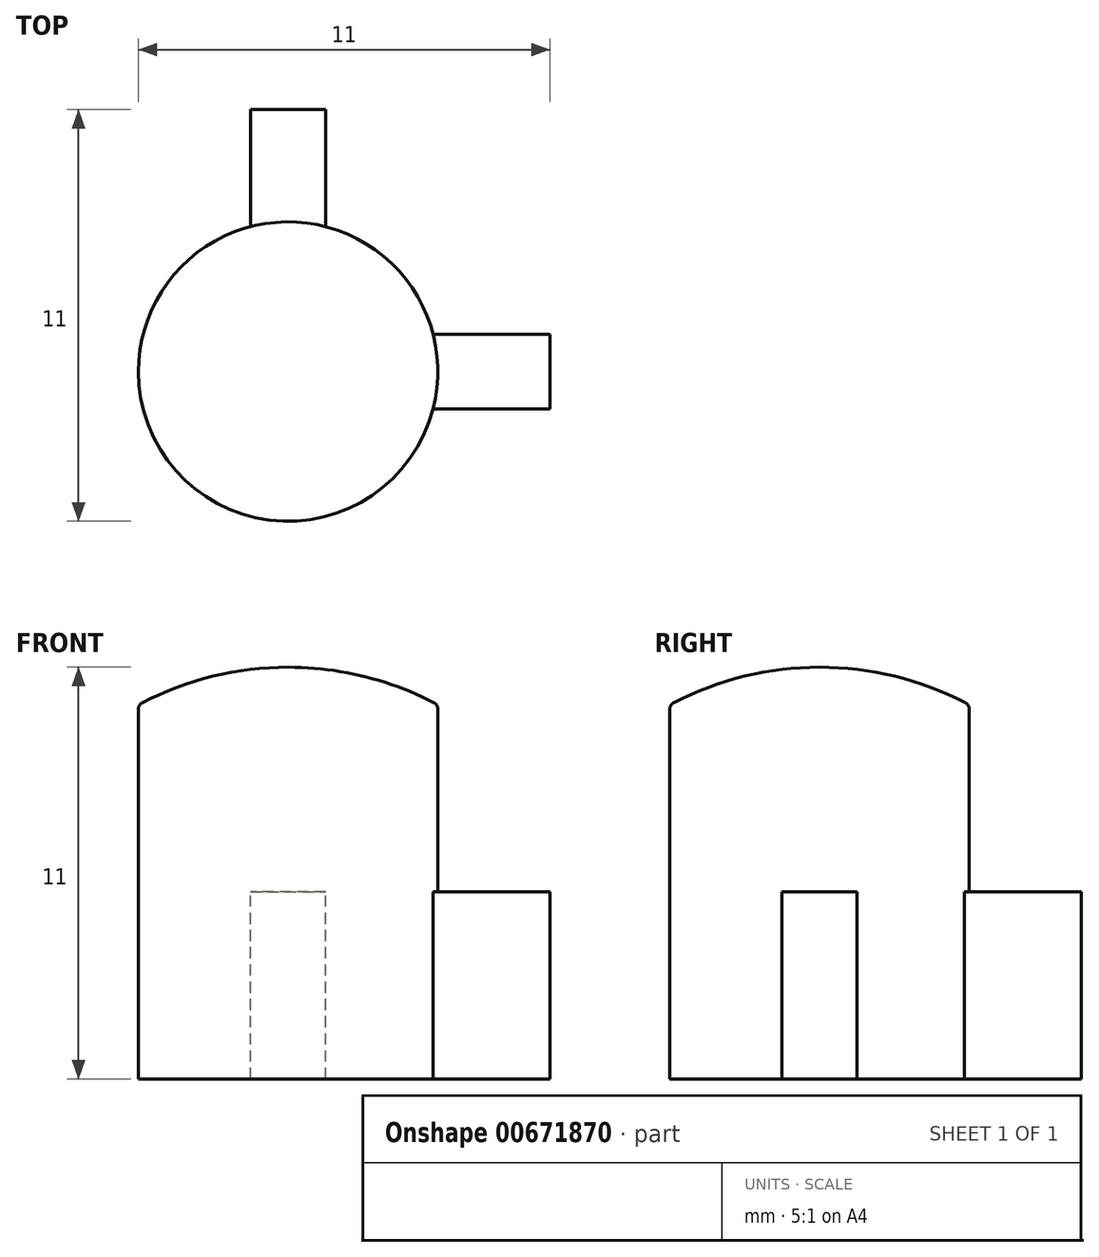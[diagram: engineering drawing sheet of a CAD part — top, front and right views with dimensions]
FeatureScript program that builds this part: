
annotation { "Feature Type Name" : "Feature", "Feature Type Description" : "" }
export const myFeature = defineFeature(function(context is Context, id is Id, definition is map)
    precondition{}
    {
        {
            var Q0;
            Q0=qCreatedBy(makeId("Front.planeOp"),FACE);
            var sketch = newSketch(context, id + "F0", { "sketchPlane" : qUnion([Q0])});
            skLineSegment(sketch, "E0", {"start": v(0, 0) * mm, "end": v(4, 0) * mm});
            skLineSegment(sketch, "E1", {"start": v(4, 0) * mm, "end": v(4, 10) * mm});
            skLineSegment(sketch, "E2", {"start": v(4, 10) * mm, "end": v(0, 10) * mm});
            skLineSegment(sketch, "E3", {"start": v(0, 10) * mm, "end": v(0, 0) * mm});
            skArc(sketch, "E4", {"start": v(0, 9.25) * mm, "mid": v(1.91, 9.44) * mm, "end": v(3.75, 10) * mm});
            skArc(sketch, "E5", {"start": v(4, 10) * mm, "mid": v(2.06, 10.75) * mm, "end": v(0, 11) * mm});
            skLineSegment(sketch, "E6", {"start": v(0, 10) * mm, "end": v(0, 11) * mm});
            skSolve(sketch);
        }
        {
            var Q0;
            {var subQ4=sQuery(id+"F0.wireOp",EDGE,"E0");Q0=makeQuery(id+"F0.imprint","IMPRINT",FACE,{"disambiguationData":[TD([[makeQuery(id+"F0.imprint","IMPRINT",EDGE,{"derivedFrom":subQ4}),1.0]])]});}
            var Q1;
            {var subQ3=sQuery(id+"F0.wireOp",EDGE,"E4");Q1=makeQuery(id+"F0.imprint","IMPRINT",FACE,{"disambiguationData":[TD([[makeQuery(id+"F0.imprint","IMPRINT",EDGE,{"derivedFrom":subQ3}),1.0]])]});}
            var Q2;
            {var subQ0=sQuery(id+"F0.wireOp",EDGE,"E5");Q2=makeQuery(id+"F0.imprint","IMPRINT",FACE,{"disambiguationData":[TD([[makeQuery(id+"F0.imprint","IMPRINT",EDGE,{"derivedFrom":subQ0}),1.0]])]});}
            var Q3;
            Q3=sQuery(id+"F0.wireOp",EDGE,"E3");
            revolve(context, id + "F1", {"entities" : qUnion([Q0, Q1, Q2]), "axis" : qUnion([Q3]), "revolveType" : RevolveType.FULL});
        }
        {
            var Q0;
            Q0=makeQuery(id+"F1.opRevolve","SWEPT_EDGE",EDGE,{"disambiguationData":[OSD([sQuery(id+"F0.wireOp",EDGE,"E2"),sQuery(id+"F0.wireOp",EDGE,"E4")])]});
            var Q1;
            Q1=makeQuery(id+"F1.opRevolve","SWEPT_EDGE",EDGE,{"disambiguationData":[OSD([sQuery(id+"F0.wireOp",EDGE,"E1"),sQuery(id+"F0.wireOp",EDGE,"E2")])]});
            fillet(context, id + "F2", {"entities" : qUnion([Q0, Q1]), "radius" : 0.2 * mm, "tangentPropagation" : true, "allowEdgeOverflow" : false});
        }
        {
            var Q0;
            Q0=qCreatedBy(makeId("Top.planeOp"),FACE);
            var sketch = newSketch(context, id + "F3", { "sketchPlane" : qUnion([Q0])});
            skLineSegment(sketch, "E7.bottom", {"start": v(-1, 0) * mm, "end": v(1, 0) * mm});
            skLineSegment(sketch, "E7.top", {"start": v(-1, 7) * mm, "end": v(1, 7) * mm});
            skLineSegment(sketch, "E7.left", {"start": v(-1, 0) * mm, "end": v(-1, 7) * mm});
            skLineSegment(sketch, "E7.right", {"start": v(1, 0) * mm, "end": v(1, 7) * mm});
            skPoint(sketch, "E7.middle", {"position": v(0, 3.5) * mm});
            skLineSegment(sketch, "E8.bottom", {"start": v(7, 1) * mm, "end": v(0, 1) * mm});
            skLineSegment(sketch, "E8.top", {"start": v(7, -1) * mm, "end": v(0, -1) * mm});
            skLineSegment(sketch, "E8.left", {"start": v(7, 1) * mm, "end": v(7, -1) * mm});
            skLineSegment(sketch, "E8.right", {"start": v(0, 1) * mm, "end": v(0, -1) * mm});
            skPoint(sketch, "E8.middle", {"position": v(3.5, 0) * mm});
            skSolve(sketch);
        }
        {
            var Q0;
            {var subQ1=sQuery(id+"F3.wireOp",EDGE,"E7.top");Q0=makeQuery(id+"F3.imprint","IMPRINT",FACE,{"disambiguationData":[TD([[makeQuery(id+"F3.imprint","IMPRINT",EDGE,{"derivedFrom":subQ1}),-1.0]])]});}
            var Q1;
            {var subQ0=sQuery(id+"F3.wireOp",EDGE,"E8.top");Q1=makeQuery(id+"F3.imprint","IMPRINT",FACE,{"disambiguationData":[TD([[makeQuery(id+"F3.imprint","IMPRINT",EDGE,{"derivedFrom":subQ0}),-1.0]])]});}
            extrude(context, id + "F4", {"entities" : qUnion([Q0, Q1]), "operationType" : NewBodyOperationType.ADD, "depth" : 5 * mm, "offsetDistance" : 25 * mm});
        }
    });
